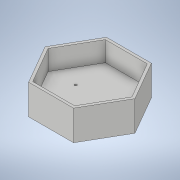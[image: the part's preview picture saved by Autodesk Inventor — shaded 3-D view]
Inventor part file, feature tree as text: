
AUTODESK INVENTOR PART (.ipt)
format: ipt  version: 2020 (Build 240168000, 168)  size: 163,840 bytes
history: native  units: in
note: dims shown in document units (in); Inventor stores cm internally (conversion verified against a paired STEP export)
features: extrude x4, sketch x4
ambient origin geometry x8: Origin, YZ Plane, XZ Plane, XY Plane, X Axis, Y Axis, Z Axis, Center Point
bodies: Solid1 (feature_tree)
feature tree (8):
  extrude  "Extrusion1"  Depth=2.25in
  extrude  "Extrusion2"  Depth=2.25in
  extrude  "Extrusion3"  Depth=1.5in
  extrude  "Extrusion4"  TaperAngle=60.0deg  [1 undecoded]
  sketch  "Sketch1"  dims[d0=2.25in d1=2.25in]
  sketch  "Sketch2"  dims[d2=2.25in d3=2.25in]
  sketch  "Sketch3"  dims[d4=1.5in d5=0.0in d6=2.1in]
  sketch  "Sketch4"  dims[d7=2.1in d8=60.0deg d9=2.1in d10=2.1in d11=1.25in d12=0.0in d13=0.25in d14=0.0in d15=0.1181in d16=0.1752in d17=0.1181in d18=1.65in d19=0.825in d20=0.1752in d21=0.1181in d22=1.7514in d23=0.825in d24=0.1181in d25=1.65in d26=1.7514in d27=0.3333in d28=0.0in]
note: 1 required parameter value undecoded (feature->parameter linkage not recoverable at this tier; creation-order binding heuristic only, values carry confidence <= 0.55)
